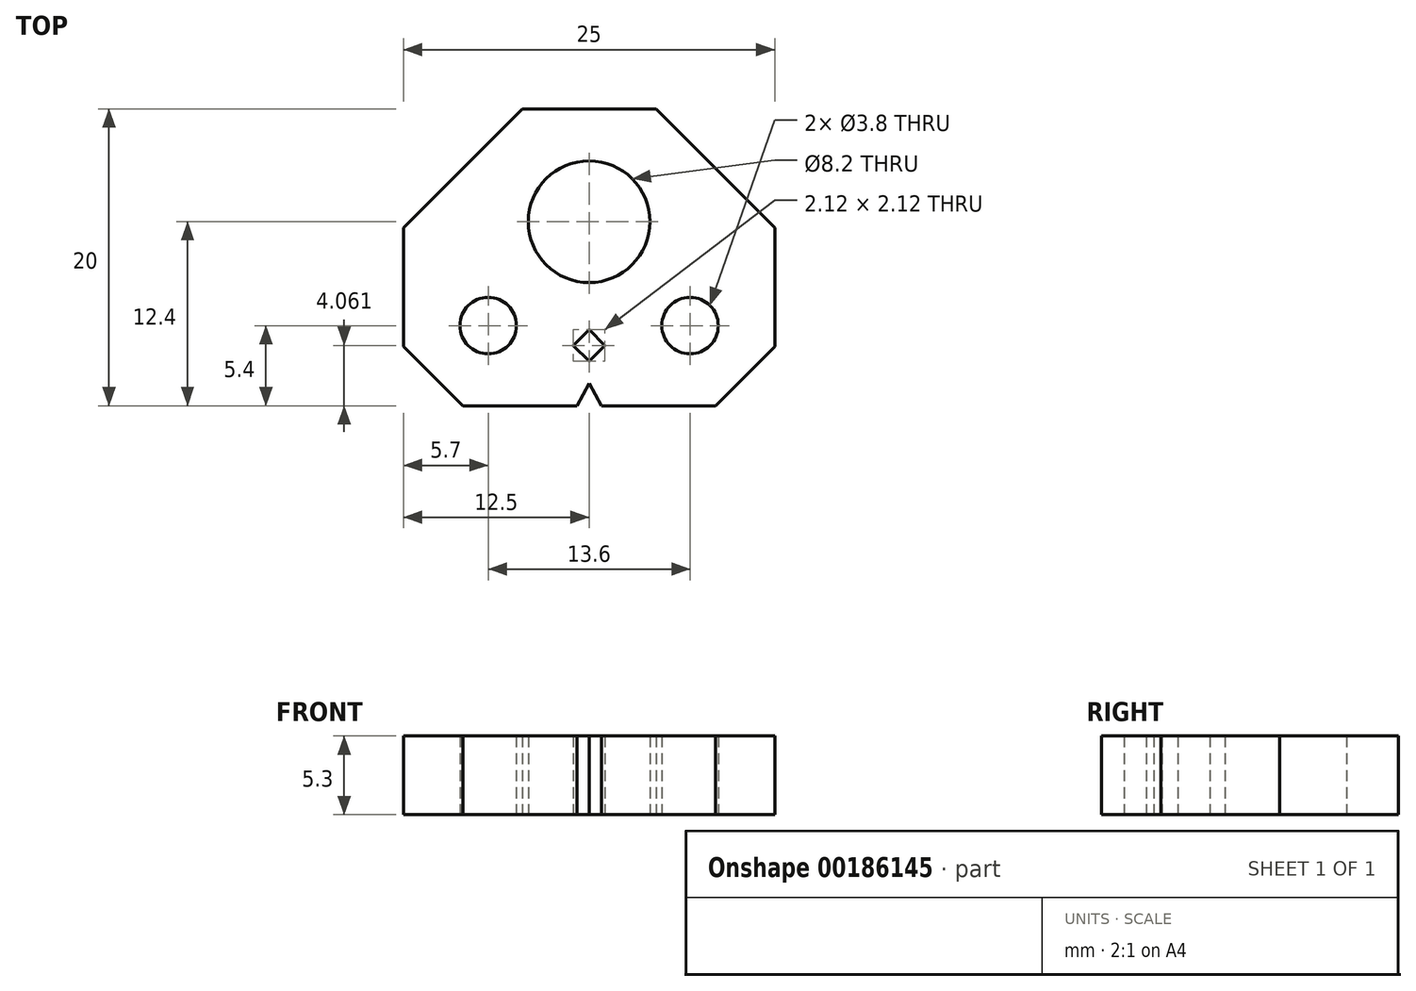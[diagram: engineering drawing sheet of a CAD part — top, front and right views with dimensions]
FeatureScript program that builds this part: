
annotation { "Feature Type Name" : "Feature", "Feature Type Description" : "" }
export const myFeature = defineFeature(function(context is Context, id is Id, definition is map)
    precondition{}
    {
        {
            var Q0;
            Q0=qCreatedBy(makeId("Top.planeOp"),FACE);
            var sketch = newSketch(context, id + "F0", { "sketchPlane" : qUnion([Q0])});
            skLineSegment(sketch, "E0.bottom", {"start": v(-4.5, 10) * mm, "end": v(4.5, 10) * mm});
            skLineSegment(sketch, "E0.top", {"start": v(-8.5, -10) * mm, "end": v(-0.83, -10) * mm});
            skLineSegment(sketch, "E0.left", {"start": v(-12.5, 2) * mm, "end": v(-12.5, -6) * mm});
            skLineSegment(sketch, "E0.right", {"start": v(12.5, 2) * mm, "end": v(12.5, -6) * mm});
            skCircle(sketch, "E1", {"center": v(0, 2.4) * mm, "radius": 4.1 * mm});
            skCircle(sketch, "E2", {"center": v(-6.8, -4.6) * mm, "radius": 1.9 * mm});
            skCircle(sketch, "E3", {"center": v(6.8, -4.6) * mm, "radius": 1.9 * mm});
            skLineSegment(sketch, "E4", {"start": v(-12.5, 2) * mm, "end": v(-4.5, 10) * mm});
            skLineSegment(sketch, "E5", {"start": v(12.5, 2) * mm, "end": v(4.5, 10) * mm});
            skPoint(sketch, "E5.endSnap0", {"position": v(0, 10) * mm});
            skLineSegment(sketch, "E6", {"start": v(-12.5, -6) * mm, "end": v(-8.5, -10) * mm});
            skLineSegment(sketch, "E7", {"start": v(8.5, -10) * mm, "end": v(12.5, -6) * mm});
            skLineSegment(sketch, "E8", {"start": v(-0.83, -10) * mm, "end": v(0, -8.5) * mm});
            skLineSegment(sketch, "E9", {"start": v(0, -8.5) * mm, "end": v(0.83, -10) * mm});
            skLineSegment(sketch, "E10", {"start": v(0, -4.88) * mm, "end": v(-1.06, -5.94) * mm});
            skLineSegment(sketch, "E11", {"start": v(-1.06, -5.94) * mm, "end": v(0, -7) * mm});
            skLineSegment(sketch, "E12", {"start": v(0, -7) * mm, "end": v(1.06, -5.94) * mm});
            skLineSegment(sketch, "E13", {"start": v(1.06, -5.94) * mm, "end": v(0, -4.88) * mm});
            skPoint(sketch, "E14.orphan", {"position": v(-12.5, 10) * mm});
            skPoint(sketch, "E15.orphan", {"position": v(12.5, 10) * mm});
            skLineSegment(sketch, "E16.trimOffspring", {"start": v(0.83, -10) * mm, "end": v(8.5, -10) * mm});
            skSolve(sketch);
        }
        {
            var Q0;
            Q0=makeQuery(id+"F0.imprint","IMPRINT",FACE,{"disambiguationData":[TD([[makeQuery(id+"F0.imprint","IMPRINT",EDGE,{"derivedFrom":sQuery(id+"F0.wireOp",EDGE,"E0.bottom")}),-1.0]])]});
            extrude(context, id + "F1", {"entities" : qUnion([Q0]), "depth" : 5.3 * mm});
        }
    });
